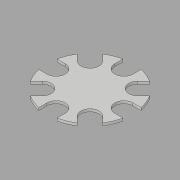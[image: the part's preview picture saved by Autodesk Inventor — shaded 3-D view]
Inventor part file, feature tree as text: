
AUTODESK INVENTOR PART (.ipt)
format: ipt  version: 2017 (Build 210142000, 142)  size: 155,648 bytes
history: native  units: in
note: dims shown in document units (in); Inventor stores cm internally (conversion verified against a paired STEP export)
features: extrude x2, sketch x2
ambient origin geometry x8: Origin, YZ Plane, XZ Plane, XY Plane, X Axis, Y Axis, Z Axis, Center Point
bodies: Solid1 (feature_tree)
feature tree (4):
  extrude  "Extrusion1"  Depth=2.75in TaperAngle=360.0deg
  extrude  "Extrusion2"  Depth=0.3937in TaperAngle=360.0deg
  sketch  "Sketch1"  dims[d0=2.75in d2=3.1496in d4=360.0deg]
  sketch  "Sketch2"  dims[d6=0.3937in d7=0.0in d8=3.1496in d10=360.0deg d12=0.3937in d13=0.0in d14=13.0in]
